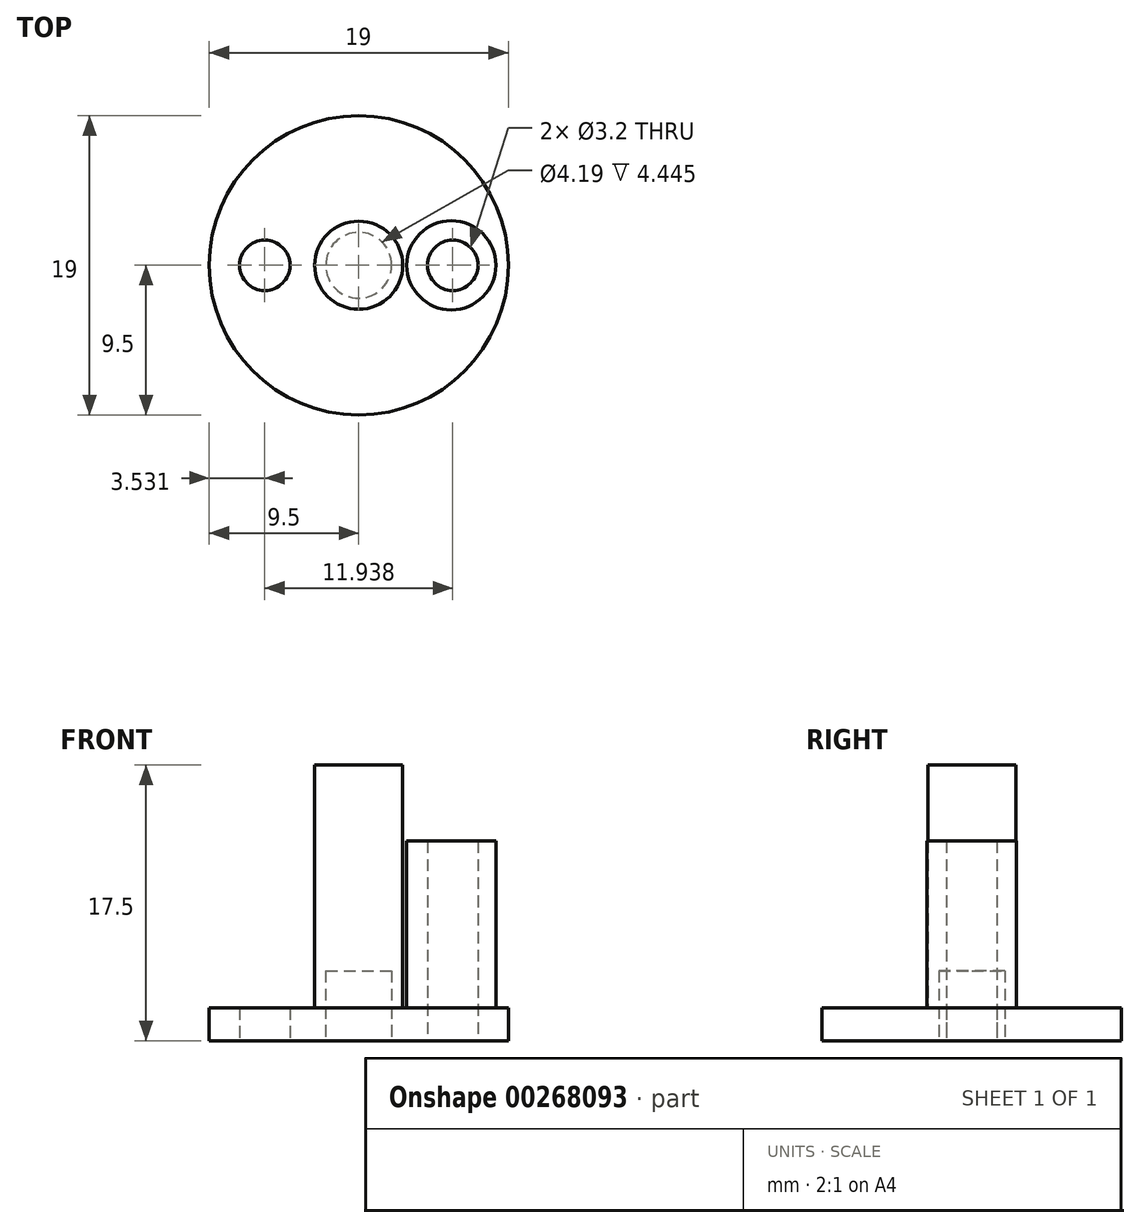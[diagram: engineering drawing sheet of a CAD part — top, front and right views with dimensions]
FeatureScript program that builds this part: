
annotation { "Feature Type Name" : "Feature", "Feature Type Description" : "" }
export const myFeature = defineFeature(function(context is Context, id is Id, definition is map)
    precondition{}
    {
        {
            var Q0;
            Q0=qCreatedBy(makeId("Top.planeOp"),FACE);
            var sketch = newSketch(context, id + "F0", { "sketchPlane" : qUnion([Q0])});
            skCircle(sketch, "E0", {"center": v(0, 0) * mm, "radius": 9.5 * mm});
            skSolve(sketch);
        }
        {
            var Q0;
            Q0=qSketchRegion(id+"F0",true);
            extrude(context, id + "F1", {"entities" : qUnion([Q0]), "depth" : 5.46 * mm});
        }
        {
            var Q0;
            Q0=makeQuery(id+"F1.opExtrude","CAP_FACE",FACE,{"disambiguationData":[OSD([sQuery(id+"F0.wireOp",EDGE,"E0")])],"isStart":false});
            var sketch = newSketch(context, id + "F2", { "sketchPlane" : qUnion([Q0])});
            skCircle(sketch, "E1", {"center": v(0, 0) * mm, "radius": 2.8 * mm});
            skSolve(sketch);
        }
        {
            var Q0;
            Q0=qSketchRegion(id+"F2",true);
            extrude(context, id + "F3", {"entities" : qUnion([Q0]), "operationType" : NewBodyOperationType.ADD, "depth" : 12.04 * mm});
        }
        {
            var Q0;
            Q0=makeQuery(id+"F1.opExtrude","CAP_FACE",FACE,{"disambiguationData":[OSD([sQuery(id+"F0.wireOp",EDGE,"E0")])],"isStart":false});
            var sketch = newSketch(context, id + "F4", { "sketchPlane" : qUnion([Q0])});
            skCircle(sketch, "E2", {"center": v(-5.88, 0) * mm, "radius": 2.83 * mm});
            skCircle(sketch, "E3.MirrorC", {"center": v(5.88, 0) * mm, "radius": 2.83 * mm});
            skSolve(sketch);
        }
        {
            var Q0;
            Q0=makeQuery(id+"F4.imprint","IMPRINT",FACE,{"disambiguationData":[TD([[makeQuery(id+"F4.imprint","IMPRINT",EDGE,{"derivedFrom":sQuery(id+"F4.wireOp",EDGE,"E2")}),1.0]])]});
            var Q1;
            Q1=makeQuery(id+"F4.imprint","IMPRINT",FACE,{"disambiguationData":[TD([[makeQuery(id+"F4.imprint","IMPRINT",EDGE,{"derivedFrom":sQuery(id+"F4.wireOp",EDGE,"E3.MirrorC")}),-1.0]])]});
            extrude(context, id + "F5", {"entities" : qUnion([Q0, Q1]), "operationType" : NewBodyOperationType.REMOVE, "oppositeDirection" : true, "depth" : 3.38 * mm});
        }
        {
            var Q0;
            Q0=makeQuery(id+"F1.opExtrude","CAP_FACE",FACE,{"disambiguationData":[OSD([sQuery(id+"F0.wireOp",EDGE,"E0")])],"isStart":true});
            var sketch = newSketch(context, id + "F6", { "sketchPlane" : qUnion([Q0])});
            skCircle(sketch, "E4", {"center": v(0, 0) * mm, "radius": 2.1 * mm});
            skSolve(sketch);
        }
        {
            var Q0;
            Q0=qSketchRegion(id+"F6",true);
            extrude(context, id + "F7", {"entities" : qUnion([Q0]), "operationType" : NewBodyOperationType.REMOVE, "oppositeDirection" : true, "depth" : 4.44 * mm});
        }
        {
            var Q0;
            Q0=makeQuery(id+"F1.opExtrude","CAP_FACE",FACE,{"disambiguationData":[OSD([sQuery(id+"F0.wireOp",EDGE,"E0")])],"isStart":true});
            var sketch = newSketch(context, id + "F8", { "sketchPlane" : qUnion([Q0])});
            skCircle(sketch, "E5", {"center": v(5.97, 0) * mm, "radius": 1.6 * mm});
            skCircle(sketch, "E6.MirrorC", {"center": v(-5.97, 0) * mm, "radius": 1.6 * mm});
            skSolve(sketch);
        }
        {
            var Q0;
            Q0=qSketchRegion(id+"F8",true);
            extrude(context, id + "F9", {"entities" : qUnion([Q0]), "operationType" : NewBodyOperationType.REMOVE, "oppositeDirection" : true, "depth" : 25.4 * mm});
        }
        {
            var Q0;
            Q0=makeQuery(id+"F1.opExtrude","CAP_FACE",FACE,{"disambiguationData":[OSD([sQuery(id+"F0.wireOp",EDGE,"E0")])],"isStart":false});
            extrude(context, id + "F10", {"entities" : qUnion([Q0]), "operationType" : NewBodyOperationType.ADD, "depth" : 7.2 * mm});
        }
    });
